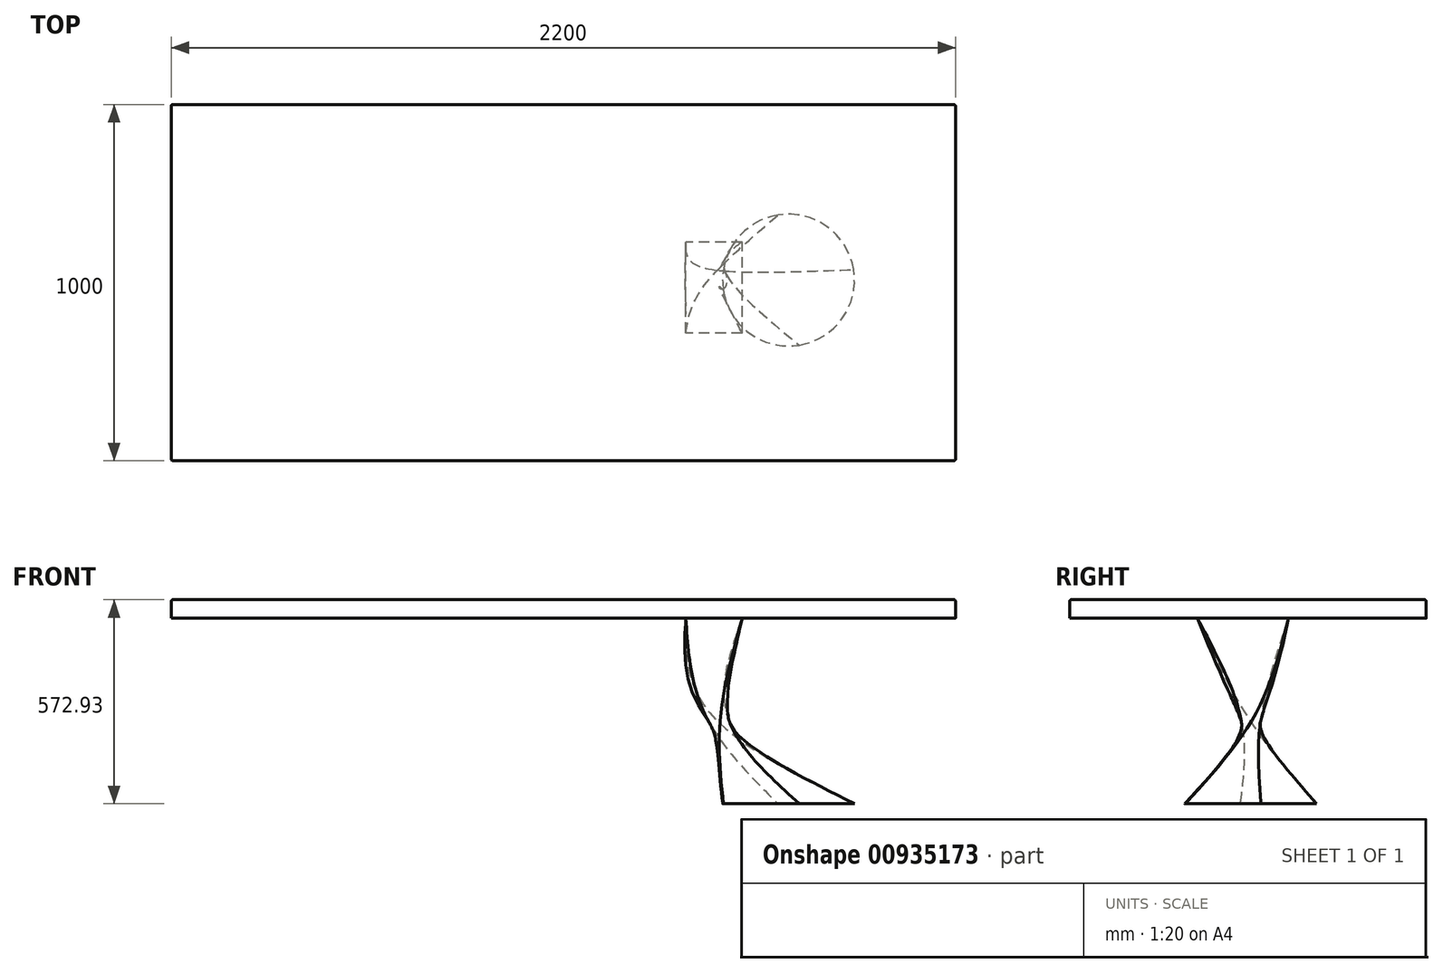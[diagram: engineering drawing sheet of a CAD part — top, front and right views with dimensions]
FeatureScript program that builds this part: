
annotation { "Feature Type Name" : "Feature", "Feature Type Description" : "" }
export const myFeature = defineFeature(function(context is Context, id is Id, definition is map)
    precondition{}
    {
        {
            var Q0;
            Q0=qCreatedBy(makeId("Top.planeOp"),FACE);
            var sketch = newSketch(context, id + "F0", { "sketchPlane" : qUnion([Q0])});
            skLineSegment(sketch, "E0.bottom", {"start": v(-994.88, 492.9) * mm, "end": v(1195.12, 492.9) * mm});
            skLineSegment(sketch, "E0.top", {"start": v(-994.88, -507.1) * mm, "end": v(1195.12, -507.1) * mm});
            skLineSegment(sketch, "E0.left", {"start": v(-999.88, 487.9) * mm, "end": v(-999.88, -502.1) * mm});
            skLineSegment(sketch, "E0.right", {"start": v(1200.12, 487.9) * mm, "end": v(1200.12, -502.1) * mm});
            skPoint(sketch, "E1.visualSharp", {"position": v(-999.88, 492.9) * mm});
            skArc(sketch, "E1.filletArc", {"start": v(-994.88, 492.9) * mm, "mid": v(-998.41, 491.44) * mm, "end": v(-999.88, 487.9) * mm});
            skPoint(sketch, "E2.visualSharp", {"position": v(-999.88, -507.1) * mm});
            skArc(sketch, "E2.filletArc", {"start": v(-999.88, -502.1) * mm, "mid": v(-998.41, -505.63) * mm, "end": v(-994.88, -507.1) * mm});
            skPoint(sketch, "E3.visualSharp", {"position": v(1200.12, -507.1) * mm});
            skArc(sketch, "E3.filletArc", {"start": v(1195.12, -507.1) * mm, "mid": v(1198.66, -505.63) * mm, "end": v(1200.12, -502.1) * mm});
            skPoint(sketch, "E4.visualSharp", {"position": v(1200.12, 492.9) * mm});
            skArc(sketch, "E4.filletArc", {"start": v(1200.12, 487.9) * mm, "mid": v(1198.66, 491.44) * mm, "end": v(1195.12, 492.9) * mm});
            skSolve(sketch);
        }
        {
            var Q0;
            Q0=makeQuery(id+"F0.imprint","IMPRINT",FACE,{"disambiguationData":[TD([[makeQuery(id+"F0.imprint","IMPRINT",EDGE,{"derivedFrom":sQuery(id+"F0.wireOp",EDGE,"E0.bottom")}),-1.0]])]});
            extrude(context, id + "F1", {"entities" : qUnion([Q0]), "depth" : 52 * mm, "offsetDistance" : 25 * mm});
        }
        {
            var Q0;
            Q0=makeQuery(id+"F1.opExtrude","CAP_FACE",FACE,{"disambiguationData":[OSD([sQuery(id+"F0.wireOp",EDGE,"E0.bottom"),sQuery(id+"F0.wireOp",EDGE,"E0.top"),sQuery(id+"F0.wireOp",EDGE,"E0.left"),sQuery(id+"F0.wireOp",EDGE,"E0.right"),sQuery(id+"F0.wireOp",EDGE,"E1.filletArc"),sQuery(id+"F0.wireOp",EDGE,"E2.filletArc"),sQuery(id+"F0.wireOp",EDGE,"E3.filletArc"),sQuery(id+"F0.wireOp",EDGE,"E4.filletArc")])],"isStart":false});
            fillet(context, id + "F2", {"entities" : qUnion([Q0]), "radius" : 5 * mm, "tangentPropagation" : true, "allowEdgeOverflow" : false});
        }
        {
            var Q0;
            Q0=qCreatedBy(makeId("Front.planeOp"),FACE);
            var sketch = newSketch(context, id + "F3", { "sketchPlane" : qUnion([Q0])});
            skFitSpline(sketch, "E5", {"points": [v(526.06, 0) * mm, v(526.06, -265.4) * mm, v(733.06, -465.22) * mm, v(742.2, -520.93) * mm], "startDerivative": vector(-175.38, -696.95) * mm, "endDerivative": vector(-47.23, -280.18) * mm});
            skSolve(sketch);
        }
        {
            var Q0;
            Q0=sQuery(id+"F3.wireOp",VERTEX,"E5.1.internal");
            var Q1;
            Q1=makeQuery(id+"F1.opExtrude","CAP_FACE",FACE,{"disambiguationData":[OSD([sQuery(id+"F0.wireOp",EDGE,"E0.bottom"),sQuery(id+"F0.wireOp",EDGE,"E0.top"),sQuery(id+"F0.wireOp",EDGE,"E0.left"),sQuery(id+"F0.wireOp",EDGE,"E0.right"),sQuery(id+"F0.wireOp",EDGE,"E1.filletArc"),sQuery(id+"F0.wireOp",EDGE,"E2.filletArc"),sQuery(id+"F0.wireOp",EDGE,"E3.filletArc"),sQuery(id+"F0.wireOp",EDGE,"E4.filletArc")])],"isStart":true});
            cPlane(context, id + "F4", {"entities" : qUnion([Q0, Q1]), "cplaneType" : CPlaneType.PLANE_POINT, "offset" : 25 * mm, "width" : 150 * mm, "height" : 150 * mm});
        }
        {
            var Q0;
            Q0=qCreatedBy(id+"F4.planeOp",FACE);
            var sketch = newSketch(context, id + "F5", { "sketchPlane" : qUnion([Q0])});
            skCircle(sketch, "E6", {"center": v(526.06, 0) * mm, "radius": 34.77 * mm});
            skSolve(sketch);
        }
        {
            var Q0;
            Q0=qCreatedBy(makeId("Top.planeOp"),FACE);
            var sketch = newSketch(context, id + "F6", { "sketchPlane" : qUnion([Q0])});
            skLineSegment(sketch, "E7.bottom", {"start": v(601.89, -148.89) * mm, "end": v(443.57, -148.89) * mm});
            skLineSegment(sketch, "E7.top", {"start": v(601.89, 106.84) * mm, "end": v(443.57, 106.84) * mm});
            skLineSegment(sketch, "E7.left", {"start": v(601.89, -148.89) * mm, "end": v(601.89, 106.84) * mm});
            skLineSegment(sketch, "E7.right", {"start": v(443.57, -148.89) * mm, "end": v(443.57, 106.84) * mm});
            skSolve(sketch);
        }
        {
            var Q0;
            Q0=sQuery(id+"F3.wireOp",VERTEX,"E5.end");
            var Q1;
            Q1=makeQuery(id+"F1.opExtrude","CAP_FACE",FACE,{"disambiguationData":[OSD([sQuery(id+"F0.wireOp",EDGE,"E0.bottom"),sQuery(id+"F0.wireOp",EDGE,"E0.top"),sQuery(id+"F0.wireOp",EDGE,"E0.left"),sQuery(id+"F0.wireOp",EDGE,"E0.right"),sQuery(id+"F0.wireOp",EDGE,"E1.filletArc"),sQuery(id+"F0.wireOp",EDGE,"E2.filletArc"),sQuery(id+"F0.wireOp",EDGE,"E3.filletArc"),sQuery(id+"F0.wireOp",EDGE,"E4.filletArc")])],"isStart":true});
            cPlane(context, id + "F7", {"entities" : qUnion([Q0, Q1]), "cplaneType" : CPlaneType.PLANE_POINT, "offset" : 25 * mm, "width" : 150 * mm, "height" : 150 * mm});
        }
        {
            var Q0;
            Q0=qCreatedBy(id+"F7.planeOp",FACE);
            var sketch = newSketch(context, id + "F8", { "sketchPlane" : qUnion([Q0])});
            skCircle(sketch, "E8", {"center": v(731.67, 0) * mm, "radius": 184.87 * mm});
            skSolve(sketch);
        }
        {
            var Q0;
            Q0=sQuery(id+"F3.wireOp",EDGE,"E5");
            var Q2;
            Q2=makeQuery(id+"F6.imprint","IMPRINT",FACE,{"disambiguationData":[TD([[makeQuery(id+"F6.imprint","IMPRINT",EDGE,{"derivedFrom":sQuery(id+"F6.wireOp",EDGE,"E7.bottom")}),-1.0]])]});
            var Q3;
            Q3=makeQuery(id+"F5.imprint","IMPRINT",FACE,{"disambiguationData":[TD([[makeQuery(id+"F5.imprint","IMPRINT",EDGE,{"derivedFrom":sQuery(id+"F5.wireOp",EDGE,"E6")}),1.0]])]});
            var Q4;
            Q4=makeQuery(id+"F8.imprint","IMPRINT",FACE,{"disambiguationData":[TD([[makeQuery(id+"F8.imprint","IMPRINT",EDGE,{"derivedFrom":sQuery(id+"F8.wireOp",EDGE,"E8")}),1.0]])]});
            loft(context, id + "F9", {"operationType" : NewBodyOperationType.ADD, "spine" : qUnion([Q0]), "sheetProfilesArray" : [{ "sheetProfileEntities" : qUnion([Q2]) }, { "sheetProfileEntities" : qUnion([Q3]) }, { "sheetProfileEntities" : qUnion([Q4]) }]});
        }
    });
